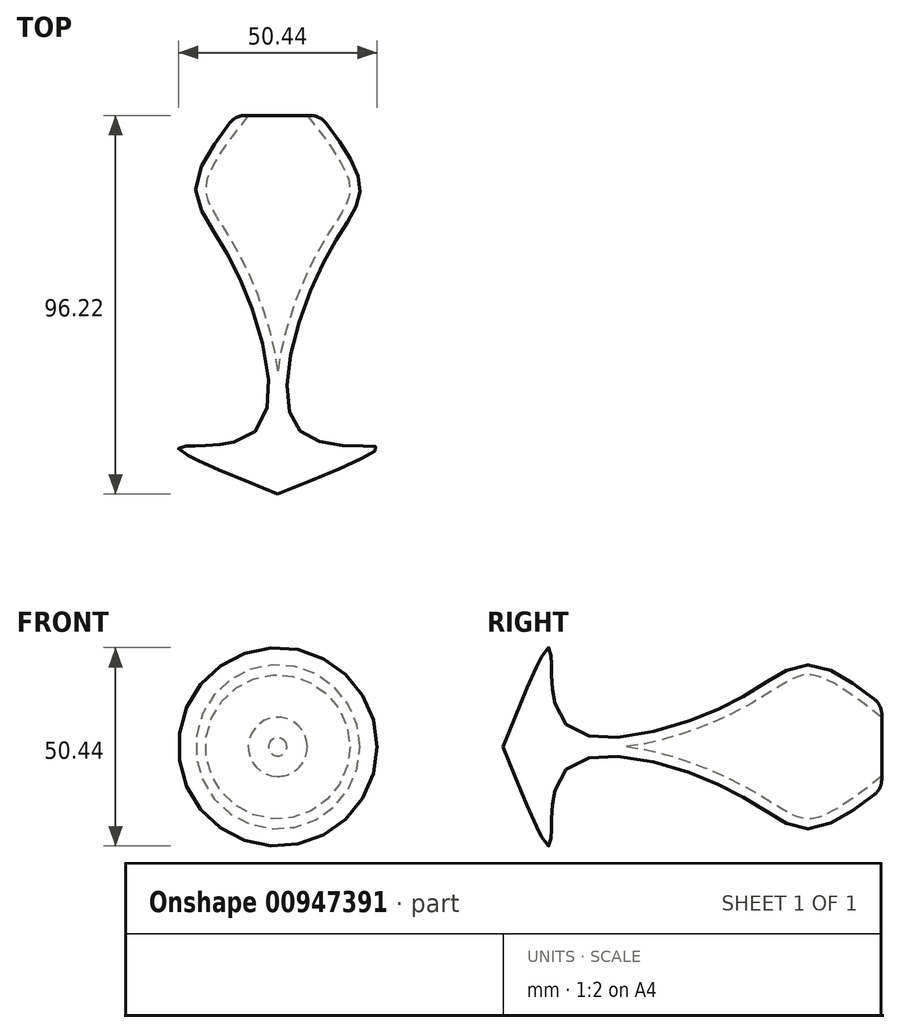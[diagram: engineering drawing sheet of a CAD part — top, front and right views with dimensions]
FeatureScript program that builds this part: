
annotation { "Feature Type Name" : "Feature", "Feature Type Description" : "" }
export const myFeature = defineFeature(function(context is Context, id is Id, definition is map)
    precondition{}
    {
        {
            var Q0;
            Q0=qCreatedBy(makeId("Top.planeOp"),FACE);
            var sketch = newSketch(context, id + "F0", { "sketchPlane" : qUnion([Q0])});
            skFitSpline(sketch, "E0", {"points": [v(10.17, 37.96) * mm, v(20.87, 18.88) * mm, v(11.64, 0) * mm, v(5.98, -43.2) * mm, v(25.06, -46.98) * mm, v(0, -58.93) * mm], "startDerivative": vector(86.05, -110.62) * mm, "endDerivative": vector(-195.24, -78.7) * mm});
            skLineSegment(sketch, "E1", {"start": v(0, -58.93) * mm, "end": v(0, 35.23) * mm});
            skLineSegment(sketch, "E2", {"start": v(0, 35.23) * mm, "end": v(10.17, 37.96) * mm});
            skSolve(sketch);
        }
        {
            var Q0;
            Q0=makeQuery(id+"F0.imprint","IMPRINT",FACE,{"disambiguationData":[TD([[makeQuery(id+"F0.imprint","IMPRINT",EDGE,{"derivedFrom":sQuery(id+"F0.wireOp",EDGE,"E0")}),-1.0]])]});
            var Q1;
            Q1=sQuery(id+"F0.wireOp",EDGE,"E1");
            revolve(context, id + "F1", {"surfaceOperationType" : NewSurfaceOperationType.NEW, "entities" : qUnion([Q0]), "axis" : qUnion([Q1]), "revolveType" : RevolveType.FULL});
        }
        {
            var Q0;
            Q0=makeQuery(id+"F1.opRevolve","SWEPT_FACE",FACE,{"disambiguationData":[OSD([sQuery(id+"F0.wireOp",EDGE,"E2")])]});
            shell(context, id + "F2", {"entities" : qUnion([Q0]), "thickness" : 2.54 * mm});
        }
        {
            var Q0;
            Q0=makeQuery(id+"F1.opRevolve","SWEPT_EDGE",EDGE,{"disambiguationData":[OSD([sQuery(id+"F0.wireOp",EDGE,"E0"),sQuery(id+"F0.wireOp",EDGE,"E2")])]});
            fillet(context, id + "F3", {"entities" : qUnion([Q0]), "radius" : 5.08 * mm, "tangentPropagation" : true, "allowEdgeOverflow" : false});
        }
    });
